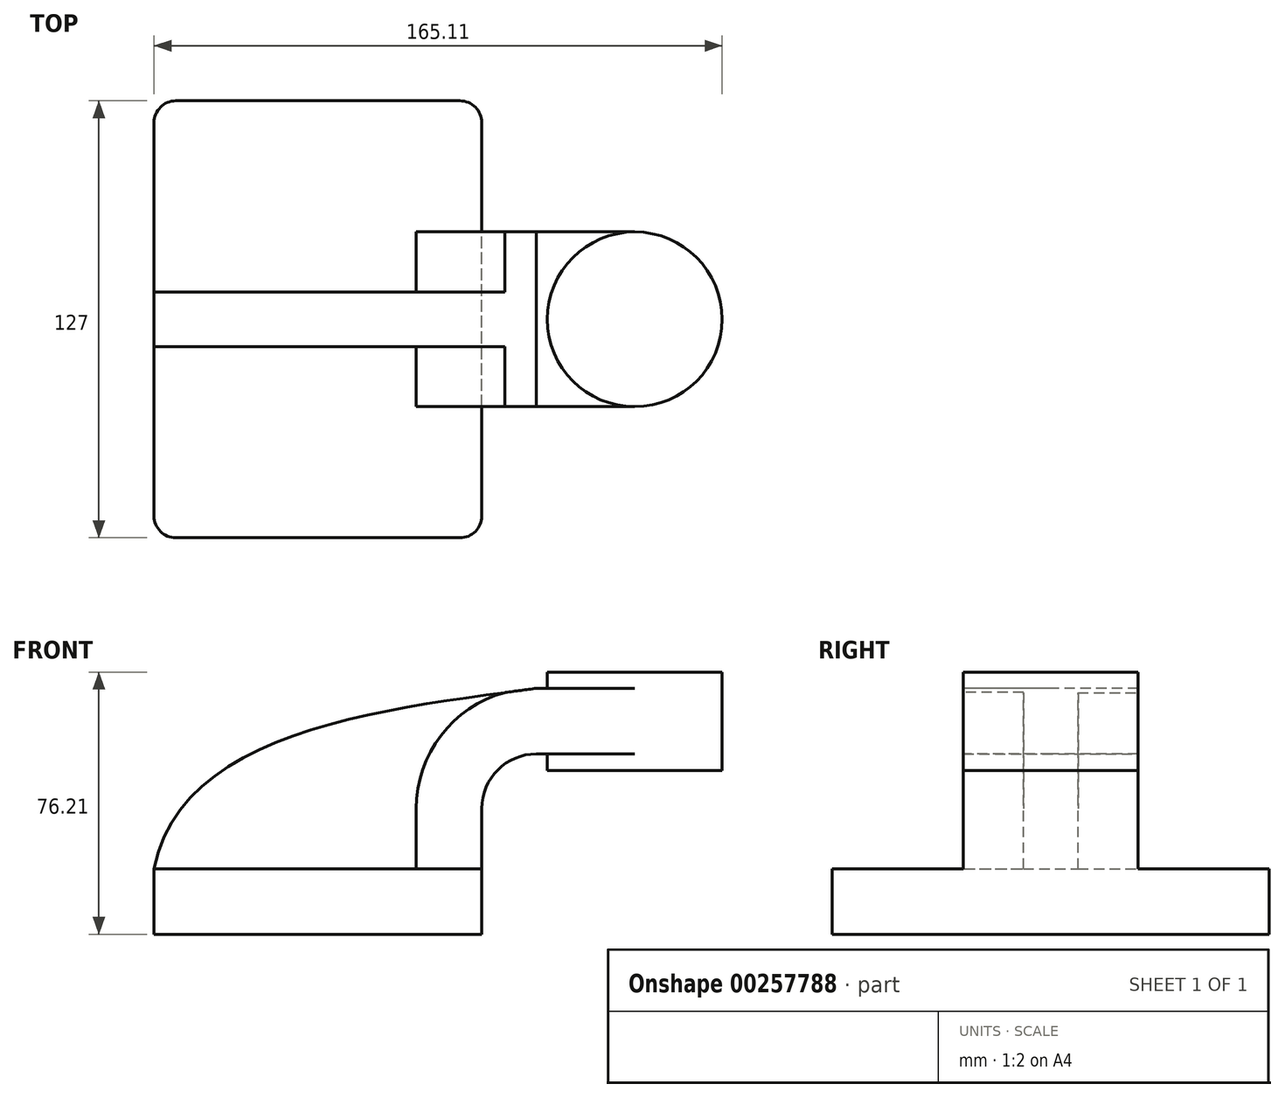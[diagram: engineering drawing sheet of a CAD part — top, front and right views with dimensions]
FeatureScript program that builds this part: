
annotation { "Feature Type Name" : "Feature", "Feature Type Description" : "" }
export const myFeature = defineFeature(function(context is Context, id is Id, definition is map)
    precondition{}
    {
        {
            var Q0;
            Q0=qCreatedBy(makeId("Front.planeOp"),FACE);
            var sketch = newSketch(context, id + "F0", { "sketchPlane" : qUnion([Q0])});
            skPoint(sketch, "E0.middle", {"position": v(0, 0) * mm});
            skLineSegment(sketch, "E1.bottom", {"start": v(47.63, -9.52) * mm, "end": v(-47.63, -9.53) * mm});
            skLineSegment(sketch, "E1.top", {"start": v(47.63, 9.53) * mm, "end": v(-47.63, 9.52) * mm});
            skLineSegment(sketch, "E1.left", {"start": v(47.63, -9.52) * mm, "end": v(47.63, 9.53) * mm});
            skLineSegment(sketch, "E1.right", {"start": v(-47.63, -9.53) * mm, "end": v(-47.63, 9.52) * mm});
            skLineSegment(sketch, "E2.bottom", {"start": v(117.48, 38.1) * mm, "end": v(66.68, 38.1) * mm});
            skLineSegment(sketch, "E2.top", {"start": v(117.48, 66.68) * mm, "end": v(66.68, 66.68) * mm});
            skLineSegment(sketch, "E2.left", {"start": v(117.48, 38.1) * mm, "end": v(117.48, 66.68) * mm});
            skLineSegment(sketch, "E2.right", {"start": v(66.68, 38.1) * mm, "end": v(66.68, 66.68) * mm});
            skPoint(sketch, "E2.middle", {"position": v(92.08, 52.39) * mm});
            skLineSegment(sketch, "E3", {"start": v(47.63, 9.53) * mm, "end": v(47.63, 27) * mm});
            skArc(sketch, "E4", {"start": v(47.62, 27) * mm, "mid": v(52.27, 38.23) * mm, "end": v(63.5, 42.88) * mm});
            skLineSegment(sketch, "E5", {"start": v(63.5, 42.88) * mm, "end": v(92.08, 42.88) * mm});
            skPoint(sketch, "E5.endSnap0", {"position": v(92.08, 38.1) * mm});
            skLineSegment(sketch, "E6.0", {"start": v(63.5, 61.93) * mm, "end": v(92.08, 61.93) * mm});
            skArc(sketch, "E6.1", {"start": v(28.58, 27) * mm, "mid": v(38.8, 51.7) * mm, "end": v(63.5, 61.93) * mm});
            skLineSegment(sketch, "E6.2", {"start": v(28.58, 9.53) * mm, "end": v(28.58, 27) * mm});
            skLineSegment(sketch, "E7", {"start": v(92.08, 38.1) * mm, "end": v(92.08, 66.68) * mm});
            skFitSpline(sketch, "E8", {"points": [v(-47.63, 9.53) * mm, v(63.5, 61.93) * mm], "startDerivative": vector(23.38, 121.42) * mm, "endDerivative": vector(131, 17.59) * mm});
            skSolve(sketch);
        }
        {
            var Q0;
            Q0=makeQuery(id+"F0.imprint","IMPRINT",FACE,{"disambiguationData":[TD([[makeQuery(id+"F0.imprint","IMPRINT",EDGE,{"derivedFrom":sQuery(id+"F0.wireOp",EDGE,"E1.bottom")}),-1.0]])]});
            extrude(context, id + "F1", {"entities" : qUnion([Q0]), "endBound" : BoundingType.SYMMETRIC, "depth" : 127 * mm});
        }
        {
            var Q0;
            {var subQ1=sQuery(id+"F0.wireOp",EDGE,"E3");Q0=makeQuery(id+"F0.imprint","IMPRINT",FACE,{"disambiguationData":[TD([[makeQuery(id+"F0.imprint","IMPRINT",EDGE,{"derivedFrom":subQ1}),1.0]])]});}
            var Q1;
            {var subQ0=sQuery(id+"F0.wireOp",EDGE,"E5");var subQ1=sQuery(id+"F0.wireOp",EDGE,"E2.right");var subQ2=makeQuery(id+"F0.imprint","INTERSECT",VERTEX,{"derivedFrom":[subQ1,subQ0]});Q1=makeQuery(id+"F0.imprint","IMPRINT",FACE,{"disambiguationData":[TD([[makeQuery(id+"F0.imprint","IMPRINT",EDGE,{"disambiguationData":[TD([[subQ2,-1.0]])],"derivedFrom":subQ1}),-1.0]])]});}
            extrude(context, id + "F2", {"entities" : qUnion([Q0, Q1]), "operationType" : NewBodyOperationType.ADD, "endBound" : BoundingType.SYMMETRIC, "depth" : 50.8 * mm});
        }
        {
            var Q0;
            {var subQ3=sQuery(id+"F0.wireOp",EDGE,"E6.2");Q0=makeQuery(id+"F0.imprint","IMPRINT",FACE,{"disambiguationData":[TD([[makeQuery(id+"F0.imprint","IMPRINT",EDGE,{"derivedFrom":subQ3}),1.0]])]});}
            extrude(context, id + "F3", {"entities" : qUnion([Q0]), "operationType" : NewBodyOperationType.ADD, "endBound" : BoundingType.SYMMETRIC, "depth" : 15.88 * mm});
        }
        {
            var Q0;
            {var subQ0=sQuery(id+"F0.wireOp",EDGE,"E2.left");Q0=makeQuery(id+"F0.imprint","IMPRINT",FACE,{"disambiguationData":[TD([[makeQuery(id+"F0.imprint","IMPRINT",EDGE,{"derivedFrom":subQ0}),1.0]])]});}
            var Q1;
            Q1=sQuery(id+"F0.wireOp",EDGE,"E7");
            revolve(context, id + "F4", {"operationType" : NewBodyOperationType.ADD, "entities" : qUnion([Q0]), "axis" : qUnion([Q1]), "revolveType" : RevolveType.FULL});
        }
        {
            var Q0;
            Q0=makeQuery(id+"F1.opExtrude","CAP_EDGE",EDGE,{"disambiguationData":[OSD([sQuery(id+"F0.wireOp",EDGE,"E1.right")])],"isStart":false});
            var Q1;
            Q1=makeQuery(id+"F1.opExtrude","CAP_EDGE",EDGE,{"disambiguationData":[OSD([sQuery(id+"F0.wireOp",EDGE,"E1.left")])],"isStart":false});
            var Q2;
            Q2=makeQuery(id+"F1.opExtrude","CAP_EDGE",EDGE,{"disambiguationData":[OSD([sQuery(id+"F0.wireOp",EDGE,"E1.left")])],"isStart":true});
            var Q3;
            Q3=makeQuery(id+"F1.opExtrude","CAP_EDGE",EDGE,{"disambiguationData":[OSD([sQuery(id+"F0.wireOp",EDGE,"E1.right")])],"isStart":true});
            fillet(context, id + "F5", {"entities" : qUnion([Q0, Q1, Q2, Q3]), "radius" : 6.35 * mm, "tangentPropagation" : true, "allowEdgeOverflow" : false});
        }
    });
